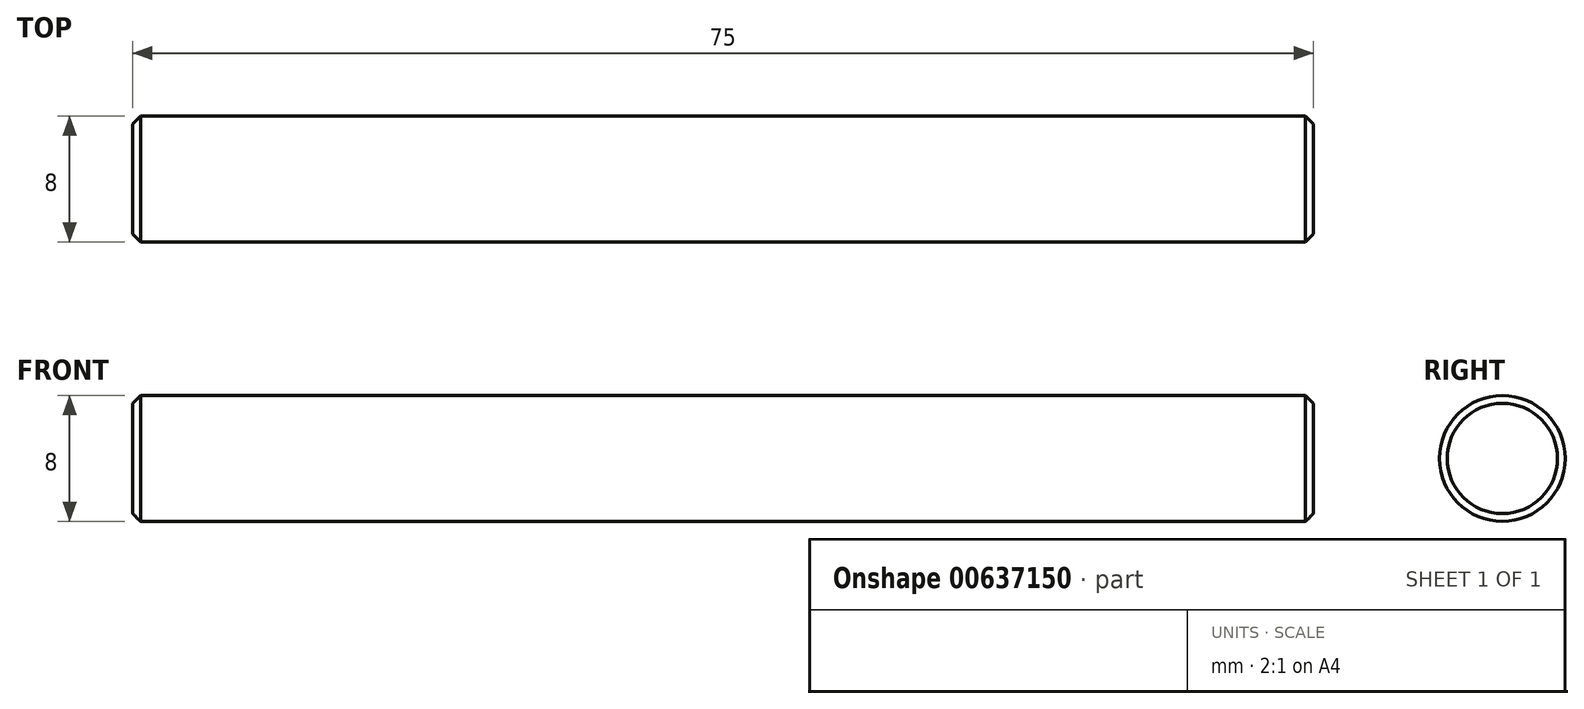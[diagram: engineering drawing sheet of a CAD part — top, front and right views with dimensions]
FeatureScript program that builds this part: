
annotation { "Feature Type Name" : "Feature", "Feature Type Description" : "" }
export const myFeature = defineFeature(function(context is Context, id is Id, definition is map)
    precondition{}
    {
        {
            var Q0;
            Q0=qCreatedBy(makeId("Right.planeOp"),FACE);
            var sketch = newSketch(context, id + "F0", { "sketchPlane" : qUnion([Q0])});
            skCircle(sketch, "E0", {"center": v(0, 0) * mm, "radius": 4 * mm});
            skSolve(sketch);
        }
        {
            var Q0;
            Q0=makeQuery(id+"F0.imprint","IMPRINT",FACE,{"disambiguationData":[TD([[makeQuery(id+"F0.imprint","IMPRINT",EDGE,{"derivedFrom":sQuery(id+"F0.wireOp",EDGE,"E0")}),1.0]])]});
            extrude(context, id + "F1", {"entities" : qUnion([Q0]), "depth" : 75 * mm, "offsetDistance" : 25 * mm});
        }
        {
            var Q0;
            Q0=makeQuery(id+"F1.opExtrude","CAP_EDGE",EDGE,{"disambiguationData":[OSD([sQuery(id+"F0.wireOp",EDGE,"E0")])],"isStart":false});
            var Q1;
            Q1=makeQuery(id+"F1.opExtrude","CAP_EDGE",EDGE,{"disambiguationData":[OSD([sQuery(id+"F0.wireOp",EDGE,"E0")])],"isStart":true});
            chamfer(context, id + "F2", {"entities" : qUnion([Q0, Q1]), "width" : .5 * mm, "tangentPropagation" : true});
        }
    });
